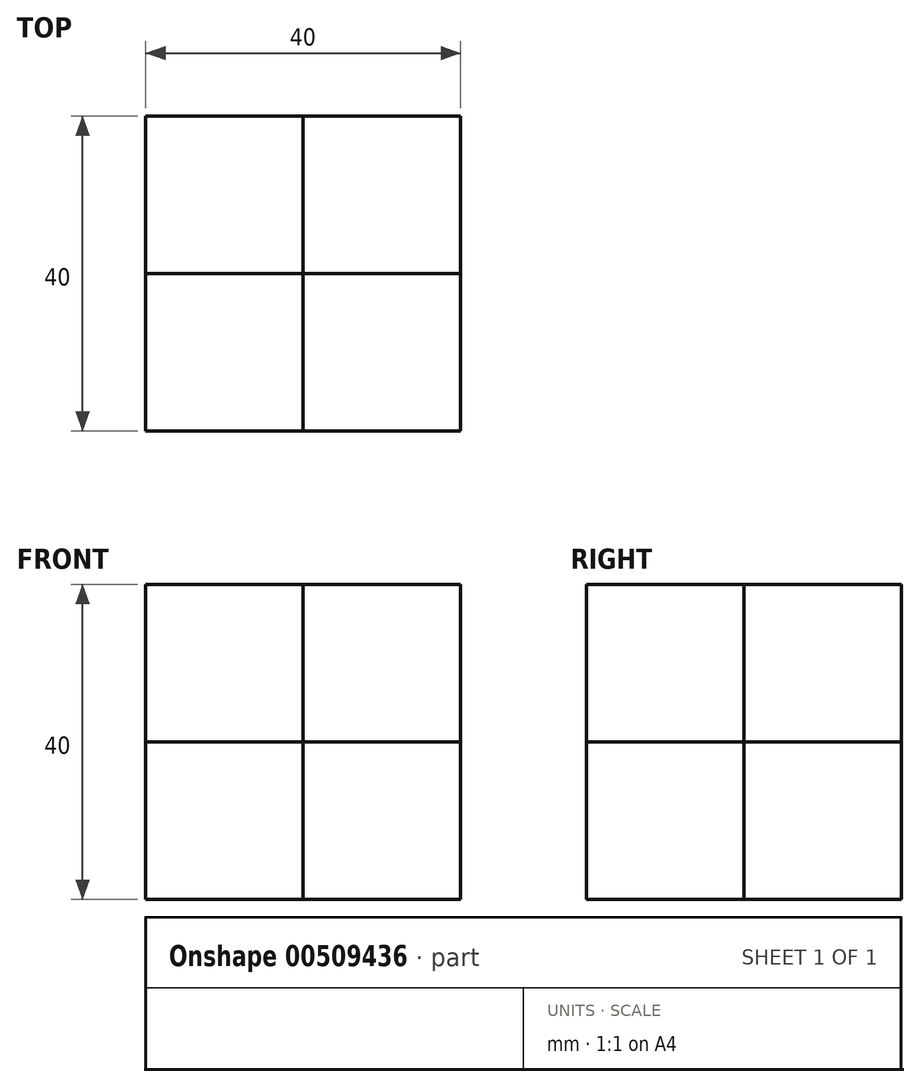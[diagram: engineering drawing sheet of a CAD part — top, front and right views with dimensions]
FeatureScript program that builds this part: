
annotation { "Feature Type Name" : "Feature", "Feature Type Description" : "" }
export const myFeature = defineFeature(function(context is Context, id is Id, definition is map)
    precondition{}
    {
        {
            var Q0;
            Q0=qCreatedBy(makeId("Top.planeOp"),FACE);
            var sketch = newSketch(context, id + "F0", { "sketchPlane" : qUnion([Q0])});
            skLineSegment(sketch, "E0.bottom", {"start": v(0, 0) * mm, "end": v(-20, 0) * mm});
            skLineSegment(sketch, "E0.top", {"start": v(0, 20) * mm, "end": v(-20, 20) * mm});
            skLineSegment(sketch, "E0.left", {"start": v(0, 0) * mm, "end": v(0, 20) * mm});
            skLineSegment(sketch, "E0.right", {"start": v(-20, 0) * mm, "end": v(-20, 20) * mm});
            skLineSegment(sketch, "E1.bottom", {"start": v(0, 0) * mm, "end": v(20, 0) * mm});
            skLineSegment(sketch, "E1.top", {"start": v(0, -20) * mm, "end": v(20, -20) * mm});
            skLineSegment(sketch, "E1.left", {"start": v(0, 0) * mm, "end": v(0, -20) * mm});
            skLineSegment(sketch, "E1.right", {"start": v(20, 0) * mm, "end": v(20, -20) * mm});
            skSolve(sketch);
        }
        {
            var Q0;
            Q0=makeQuery(id+"F0.imprint","IMPRINT",FACE,{"disambiguationData":[TD([[makeQuery(id+"F0.imprint","IMPRINT",EDGE,{"derivedFrom":sQuery(id+"F0.wireOp",EDGE,"E0.bottom")}),-1.0]])]});
            var Q1;
            Q1=makeQuery(id+"F0.imprint","IMPRINT",FACE,{"disambiguationData":[TD([[makeQuery(id+"F0.imprint","IMPRINT",EDGE,{"derivedFrom":sQuery(id+"F0.wireOp",EDGE,"E1.bottom")}),-1.0]])]});
            extrude(context, id + "F1", {"entities" : qUnion([Q0, Q1]), "depth" : 20 * mm});
        }
        {
            var Q0;
            Q0=qCreatedBy(makeId("Top.planeOp"),FACE);
            var sketch = newSketch(context, id + "F2", { "sketchPlane" : qUnion([Q0])});
            skLineSegment(sketch, "E2.bottom", {"start": v(0, 0) * mm, "end": v(20, 0) * mm});
            skLineSegment(sketch, "E2.top", {"start": v(0, 20) * mm, "end": v(20, 20) * mm});
            skLineSegment(sketch, "E2.left", {"start": v(0, 0) * mm, "end": v(0, 20) * mm});
            skLineSegment(sketch, "E2.right", {"start": v(20, 0) * mm, "end": v(20, 20) * mm});
            skLineSegment(sketch, "E3.bottom", {"start": v(0, 0) * mm, "end": v(-20, 0) * mm});
            skLineSegment(sketch, "E3.top", {"start": v(0, -20) * mm, "end": v(-20, -20) * mm});
            skLineSegment(sketch, "E3.left", {"start": v(0, 0) * mm, "end": v(0, -20) * mm});
            skLineSegment(sketch, "E3.right", {"start": v(-20, 0) * mm, "end": v(-20, -20) * mm});
            skSolve(sketch);
        }
        {
            var Q0;
            Q0=makeQuery(id+"F2.imprint","IMPRINT",FACE,{"disambiguationData":[TD([[makeQuery(id+"F2.imprint","IMPRINT",EDGE,{"derivedFrom":sQuery(id+"F2.wireOp",EDGE,"E2.bottom")}),1.0]])]});
            var Q1;
            Q1=makeQuery(id+"F2.imprint","IMPRINT",FACE,{"disambiguationData":[TD([[makeQuery(id+"F2.imprint","IMPRINT",EDGE,{"derivedFrom":sQuery(id+"F2.wireOp",EDGE,"E3.bottom")}),1.0]])]});
            extrude(context, id + "F3", {"entities" : qUnion([Q0, Q1]), "depth" : 20 * mm});
        }
        {
            var Q0;
            Q0=makeQuery(id+"F1.opExtrude","CAP_FACE",FACE,{"disambiguationData":[OSD([sQuery(id+"F0.wireOp",EDGE,"E0.bottom"),sQuery(id+"F0.wireOp",EDGE,"E0.top"),sQuery(id+"F0.wireOp",EDGE,"E0.left"),sQuery(id+"F0.wireOp",EDGE,"E0.right")])],"isStart":false});
            var sketch = newSketch(context, id + "F4", { "sketchPlane" : qUnion([Q0])});
            skLineSegment(sketch, "E4.bottom", {"start": v(0, 0) * mm, "end": v(-20, 0) * mm});
            skLineSegment(sketch, "E4.top", {"start": v(0, 20) * mm, "end": v(-20, 20) * mm});
            skLineSegment(sketch, "E4.left", {"start": v(0, 0) * mm, "end": v(0, 20) * mm});
            skLineSegment(sketch, "E4.right", {"start": v(-20, 0) * mm, "end": v(-20, 20) * mm});
            skLineSegment(sketch, "E5.bottom", {"start": v(0, 0) * mm, "end": v(20, 0) * mm});
            skLineSegment(sketch, "E5.top", {"start": v(0, 20) * mm, "end": v(20, 20) * mm});
            skLineSegment(sketch, "E5.right", {"start": v(20, 0) * mm, "end": v(20, 20) * mm});
            skLineSegment(sketch, "E6.top", {"start": v(0, -20) * mm, "end": v(20, -20) * mm});
            skLineSegment(sketch, "E6.left", {"start": v(0, 0) * mm, "end": v(0, -20) * mm});
            skLineSegment(sketch, "E6.right", {"start": v(20, 0) * mm, "end": v(20, -20) * mm});
            skLineSegment(sketch, "E7.top", {"start": v(0, -20) * mm, "end": v(-20, -20) * mm});
            skLineSegment(sketch, "E7.right", {"start": v(-20, 0) * mm, "end": v(-20, -20) * mm});
            skSolve(sketch);
        }
        {
            var Q0;
            Q0=makeQuery(id+"F4.imprint","IMPRINT",FACE,{"disambiguationData":[TD([[makeQuery(id+"F4.imprint","IMPRINT",EDGE,{"derivedFrom":sQuery(id+"F4.wireOp",EDGE,"E4.top")}),1.0]])]});
            var Q1;
            Q1=makeQuery(id+"F4.imprint","IMPRINT",FACE,{"disambiguationData":[TD([[makeQuery(id+"F4.imprint","IMPRINT",EDGE,{"derivedFrom":sQuery(id+"F4.wireOp",EDGE,"E5.bottom")}),-1.0]])]});
            extrude(context, id + "F5", {"entities" : qUnion([Q0, Q1]), "depth" : 20 * mm});
        }
        {
            var Q0;
            Q0=makeQuery(id+"F3.opExtrude","CAP_FACE",FACE,{"disambiguationData":[OSD([sQuery(id+"F2.wireOp",EDGE,"E3.bottom"),sQuery(id+"F2.wireOp",EDGE,"E3.top"),sQuery(id+"F2.wireOp",EDGE,"E3.left"),sQuery(id+"F2.wireOp",EDGE,"E3.right")])],"isStart":false});
            var Q1;
            Q1=makeQuery(id+"F3.opExtrude","CAP_FACE",FACE,{"disambiguationData":[OSD([sQuery(id+"F2.wireOp",EDGE,"E2.bottom"),sQuery(id+"F2.wireOp",EDGE,"E2.top"),sQuery(id+"F2.wireOp",EDGE,"E2.left"),sQuery(id+"F2.wireOp",EDGE,"E2.right")])],"isStart":false});
            extrude(context, id + "F6", {"entities" : qUnion([Q0, Q1]), "depth" : 20 * mm});
        }
    });
